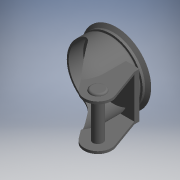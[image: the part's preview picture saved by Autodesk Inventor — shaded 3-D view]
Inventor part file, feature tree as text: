
AUTODESK INVENTOR PART (.ipt)
format: ipt  version: 2017.3 (Build 213256000, 256)  size: 246,784 bytes
history: native  units: mm (DEFAULTED — no unit token found)
features: sketch x10, extrude x7, revolve x3
ambient origin geometry x8: Origin, YZ Plane, XZ Plane, XY Plane, X Axis, Y Axis, Z Axis, Center Point
bodies: Solid1 (feature_tree), body_to_dummy_XY (feature_tree), body_to_dummy_YZ (feature_tree), body_to_dummy_ZX (feature_tree), body_to_dummy_X (feature_tree), body_to_dummy_Y (feature_tree), body_to_dummy_Z (feature_tree), body_to_dummy_Center (feature_tree), body_to_stopper_left_XY (feature_tree), body_to_stopper_left_YZ (feature_tree), body_to_stopper_left_ZX (feature_tree), body_to_stopper_left_X (feature_tree), body_to_stopper_left_Y (feature_tree), body_to_stopper_left_Z (feature_tree), body_to_stopper_left_Center (feature_tree), body_to_stopper_right_XY (feature_tree), body_to_stopper_right_YZ (feature_tree), body_to_stopper_right_ZX (feature_tree), body_to_stopper_right_X (feature_tree), body_to_stopper_right_Y (feature_tree), body_to_stopper_right_Z (feature_tree), body_to_stopper_right_Center (feature_tree), body_to_swivel_XY (feature_tree), body_to_swivel_YZ (feature_tree), body_to_swivel_ZX (feature_tree), body_to_swivel_X (feature_tree), body_to_swivel_Y (feature_tree), body_to_swivel_Z (feature_tree), body_to_swivel_Center (feature_tree), body_to_wheel_XY (feature_tree), body_to_wheel_YZ (feature_tree), body_to_wheel_ZX (feature_tree), body_to_wheel_X (feature_tree), body_to_wheel_Y (feature_tree), body_to_wheel_Z (feature_tree), body_to_wheel_Center (feature_tree)
feature tree (20):
  revolve  "Revolution1"  [1 undecoded]
  extrude  "Extrusion1"  Depth=100.0mm TaperAngle=0.0deg
  sketch  "Sketch_3"  dims[d7=24.076mm d8=0.0mm d9=360.0deg]
  extrude  "Extrusion2"  TaperAngle=360.0deg  [1 undecoded]
  extrude  "Extrusion3"  Depth=116.0mm TaperAngle=0.0deg
  extrude  "Extrusion4"  TaperAngle=360.0deg  [1 undecoded]
  revolve  "Revolution2"  [1 undecoded]
  extrude  "Extrusion5"  [1 undecoded]
  extrude  "Extrusion6"  [1 undecoded]
  extrude  "Extrusion7"  [1 undecoded]
  revolve  "Revolution3"  [1 undecoded]
  sketch  "Sketch_1"  dims[d0=360.0deg d1=56.0mm d2=0.0mm]
  sketch  "Sketch_2"  dims[d3=44.0mm d4=0.0mm d5=100.0mm d6=0.0mm]
  sketch  "Sketch_5"  dims[d14=36.6mm d15=0.0mm d16=360.0deg]
  sketch  "Sketch_4"  dims[d10=116.0mm d11=0.0mm d12=116.0mm d13=0.0mm]
  sketch  "Sketch_6"  dims[d17=0.0mm d18=0.0mm d19=0.0mm]
  sketch  "Sketch_7"
  sketch  "Sketch_8"
  sketch  "Sketch_9"
  sketch  "Sketch_10"
note: 8 required parameter values undecoded (feature->parameter linkage not recoverable at this tier; creation-order binding heuristic only, values carry confidence <= 0.55)